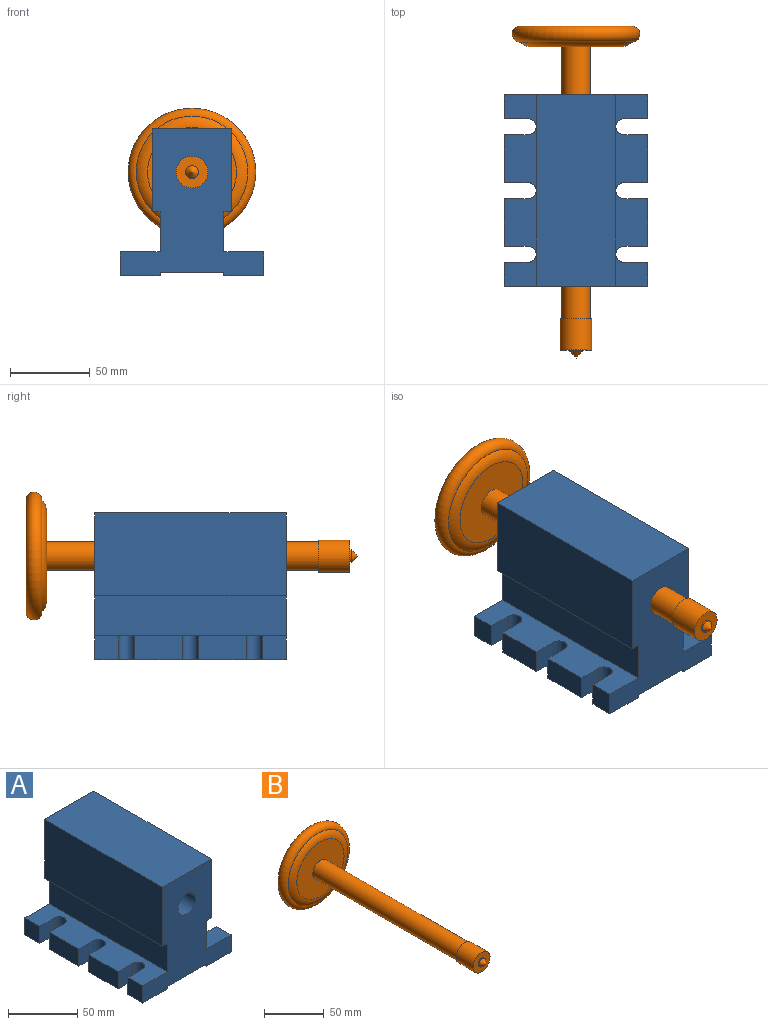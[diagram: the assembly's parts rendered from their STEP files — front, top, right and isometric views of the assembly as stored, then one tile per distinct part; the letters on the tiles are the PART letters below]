
ASSEMBLY  parts=2 mates=1
PART A: 43 faces, bbox 90x120x92 mm
  f0: plane 120x2mm, normal (-1,0,0), area 240mm2, adj f2,f3,f17,f36
  f1: plane 15x15mm, normal (1,0,0), area 225mm2, adj f2,f15,f16,f17
  f2: plane 92x90mm, normal (0,1,0), area 4615.5mm2, adj f0,f1,f16,f17,f18,f19,f20,f33
  f3: plane 92x90mm, normal (0,-1,0), area 4615.5mm2, adj f0,f4,f16,f17,f18,f19,f32,f33
  f4: plane 15x15mm, normal (1,0,0), area 225mm2, adj f3,f5,f16,f17
  f5: plane 15x15mm, normal (0,1,0), area 225mm2, adj f4,f6,f16,f17
  f6: cylinder r=5mm len=15mm, axis (0,0,-1), area 235.6mm2, adj f5,f7,f16,f17
  f7: plane 15x15mm, normal (0,-1,0), area 225mm2, adj f6,f8,f16,f17
  f8: plane 30x15mm, normal (1,0,0), area 450mm2, adj f7,f9,f16,f17
  f9: plane 15x15mm, normal (0,1,0), area 225mm2, adj f8,f10,f16,f17
  f10: cylinder r=5mm len=15mm, axis (0,0,-1), area 235.6mm2, adj f9,f11,f16,f17
  f11: plane 15x15mm, normal (0,-1,0), area 225mm2, adj f10,f12,f16,f17
  f12: plane 30x15mm, normal (1,0,0), area 450mm2, adj f11,f13,f16,f17
  f13: plane 15x15mm, normal (0,1,0), area 225mm2, adj f12,f14,f16,f17
  f14: cylinder r=5mm len=15mm, axis (0,0,-1), area 235.6mm2, adj f13,f15,f16,f17
  f15: plane 15x15mm, normal (0,-1,0), area 225mm2, adj f1,f14,f16,f17
  f16: plane 120x25mm, normal (0,0,1), area 2432.2mm2, adj f1,f2,f3,f4,f5,f6,f7,f8
  f17: plane 120x25mm, normal (0,0,-1), area 2432.2mm2, adj f0,f1,f2,f3,f4,f5,f6,f7
  f18: plane 120x25mm, normal (1,0,0), area 3000mm2, adj f2,f3,f16,f37
  f19: plane 120x2mm, normal (1,0,0), area 240mm2, adj f2,f3,f34,f36
  f20: plane 15x15mm, normal (-1,0,0), area 225mm2, adj f2,f21,f33,f34
  f21: plane 15x15mm, normal (0,-1,0), area 225mm2, adj f20,f22,f33,f34
  f22: cylinder r=5mm len=15mm, axis (0,0,-1), area 235.6mm2, adj f21,f23,f33,f34
  f23: plane 15x15mm, normal (0,1,0), area 225mm2, adj f22,f24,f33,f34
  f24: plane 30x15mm, normal (-1,0,0), area 450mm2, adj f23,f25,f33,f34
  f25: plane 15x15mm, normal (0,-1,0), area 225mm2, adj f24,f26,f33,f34
  f26: cylinder r=5mm len=15mm, axis (0,0,-1), area 235.6mm2, adj f25,f27,f33,f34
  f27: plane 15x15mm, normal (0,1,0), area 225mm2, adj f26,f28,f33,f34
  f28: plane 30x15mm, normal (-1,0,0), area 450mm2, adj f27,f29,f33,f34
  f29: plane 15x15mm, normal (0,-1,0), area 225mm2, adj f28,f30,f33,f34
  f30: cylinder r=5mm len=15mm, axis (0,0,-1), area 235.6mm2, adj f29,f31,f33,f34
  f31: plane 15x15mm, normal (0,1,0), area 225mm2, adj f30,f32,f33,f34
  f32: plane 15x15mm, normal (-1,0,0), area 225mm2, adj f3,f31,f33,f34
  f33: plane 120x25mm, normal (0,0,1), area 2432.2mm2, adj f2,f3,f20,f21,f22,f23,f24,f25
  f34: plane 120x25mm, normal (0,0,-1), area 2432.2mm2, adj f2,f3,f19,f20,f21,f22,f23,f24
  f35: plane 120x25mm, normal (-1,0,0), area 3000mm2, adj f2,f3,f33,f41
  f36: plane 120x40mm, normal (0,0,-1), area 4800mm2, adj f0,f2,f3,f19
  f37: plane 120x5mm, normal (0,0,-1), area 600mm2, adj f2,f3,f18,f38
  f38: plane 120x52mm, normal (1,0,0), area 6240mm2, adj f2,f3,f37,f40
  f39: plane 120x52mm, normal (-1,0,0), area 6240mm2, adj f2,f3,f40,f41
  f40: plane 120x50mm, normal (0,0,1), area 6000mm2, adj f2,f3,f38,f39
  f41: plane 120x5mm, normal (0,0,-1), area 600mm2, adj f2,f3,f35,f39
  f42: cylinder r=9mm len=120mm, axis (0,-1,0), area 6785.8mm2, adj f2,f3
PART B: 11 faces, bbox 86.6x212x86.6 mm
  f0: cylinder r=9mm len=170mm, axis (0,-1,0), area 9613.3mm2, adj f3,f8
  f1: cylinder r=10mm len=20mm, axis (0,1,0), area 1256.6mm2, adj f2,f3
  f2: plane 20x20mm, normal (0,-1,0), area 263.9mm2, adj f1,f4
  f3: plane 20x20mm, normal (0,1,0), area 59.7mm2, adj f0,f1
  f4: cylinder r=4mm len=8mm, axis (0,1,0), area 25.1mm2, adj f2,f5
  f5: cone r=4mm half-angle=45deg, axis (0,1,0), area 71.1mm2, adj f4
  f6: torus R=35mm, axis (0,1,0), area 4725.3mm2, adj f9,f10
  f7: plane 46x46mm, normal (0,1,0), area 1661.9mm2, adj f9
  f8: plane 55.72x55.72mm, normal (0,-1,0), area 2183.7mm2, adj f0,f10
  f9: torus R=23mm, axis (0,-1,0), area 1591.4mm2, adj f6,f7
  f10: torus R=27.86mm, axis (0,-1,0), area 1580.8mm2, adj f6,f8
PLACE A at identity
PLACE B at identity
MATE revolute B.f0 <-> A.f42  axis (0,1,0) through (0,-80,65)mm
